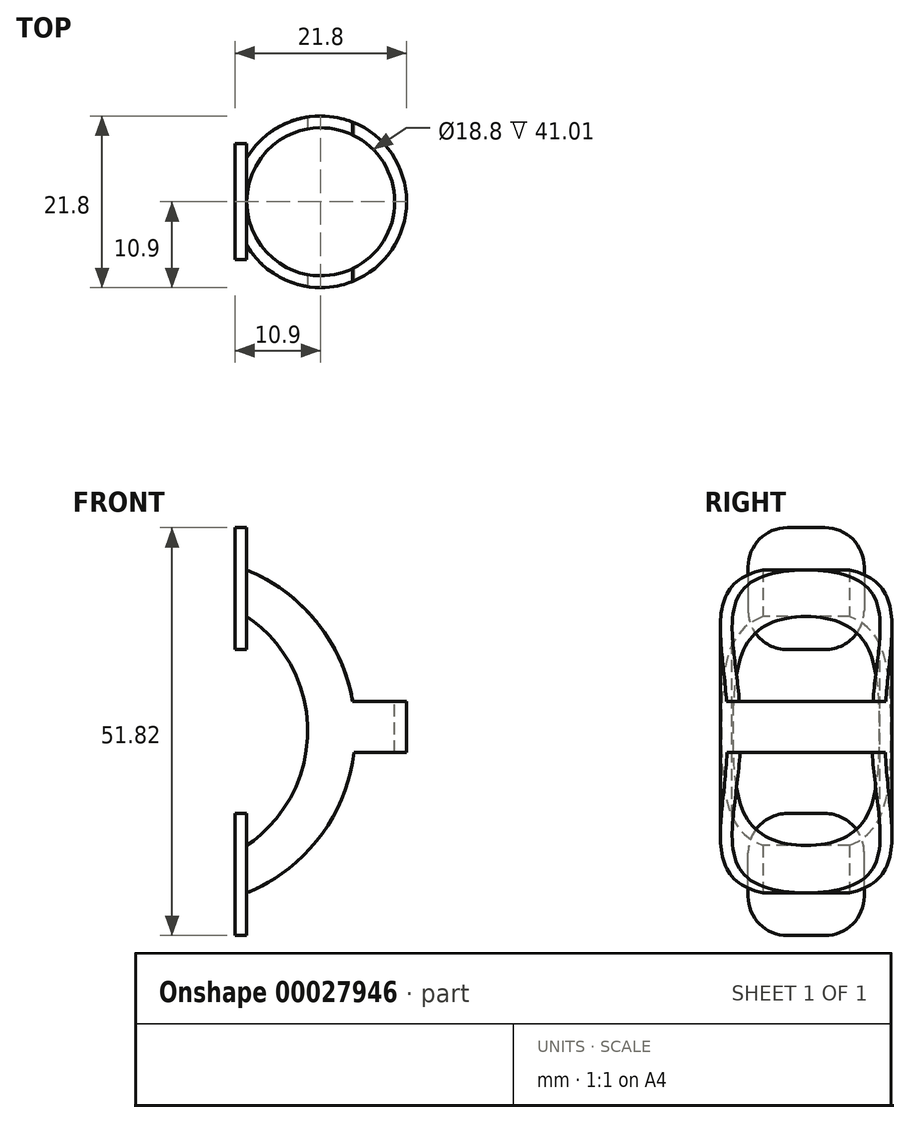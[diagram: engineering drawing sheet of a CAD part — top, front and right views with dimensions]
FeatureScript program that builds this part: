
annotation { "Feature Type Name" : "Feature", "Feature Type Description" : "" }
export const myFeature = defineFeature(function(context is Context, id is Id, definition is map)
    precondition{}
    {
        {
            var Q0;
            Q0=qCreatedBy(makeId("Top.planeOp"),FACE);
            var sketch = newSketch(context, id + "F0", { "sketchPlane" : qUnion([Q0])});
            skCircle(sketch, "E0", {"center": v(0, 0) * mm, "radius": 10.9 * mm});
            skSolve(sketch);
        }
        {
            var Q0;
            Q0 = qSketchRegion(id + "F0", true);
            extrude(context, id + "F1", {"entities" : qUnion([Q0]), "depth" : 42 * mm});
        }
        {
            var Q0;
            Q0=makeQuery(id+"F1.opExtrude","CAP_FACE",FACE,{"disambiguationData":[OSD([sQuery(id+"F0.wireOp",EDGE,"E0")])],"isStart":false});
            var sketch = newSketch(context, id + "F2", { "sketchPlane" : qUnion([Q0])});
            skCircle(sketch, "E1.0", {"center": v(0, 0) * mm, "radius": 9.4 * mm});
            skSolve(sketch);
        }
        {
            var Q0;
            Q0=makeQuery(id+"F2.imprint","IMPRINT",FACE,{"disambiguationData":[TD([[makeQuery(id+"F2.imprint","IMPRINT",EDGE,{"derivedFrom":sQuery(id+"F2.wireOp",EDGE,"E1.0")}),1.0]])]});
            extrude(context, id + "F3", {"entities" : qUnion([Q0]), "operationType" : NewBodyOperationType.REMOVE, "endBound" : BoundingType.THROUGH_ALL, "oppositeDirection" : true, "depth" : 25 * mm});
        }
        {
            var Q0;
            Q0=qCreatedBy(makeId("Front.planeOp"),FACE);
            cPlane(context, id + "F4", {"entities" : qUnion([Q0]), "cplaneType" : CPlaneType.OFFSET, "offset" : 10.9 * mm, "width" : 150 * mm, "height" : 150 * mm});
        }
        {
            var Q0;
            Q0=qCreatedBy(makeId("Front.planeOp"),FACE);
            var sketch = newSketch(context, id + "F5", { "sketchPlane" : qUnion([Q0])});
            skArc(sketch, "E2", {"start": v(-11.41, 5.25) * mm, "mid": v(-1.67, 21.04) * mm, "end": v(-11.54, 36.75) * mm});
            skLineSegment(sketch, "E3", {"start": v(-11.54, 36.75) * mm, "end": v(-11.41, 5.25) * mm});
            skSolve(sketch);
        }
        {
            var Q0;
            Q0=makeQuery(id+"F5.imprint","IMPRINT",FACE,{"disambiguationData":[TD([[makeQuery(id+"F5.imprint","IMPRINT",EDGE,{"derivedFrom":sQuery(id+"F5.wireOp",EDGE,"E2")}),1.0]])]});
            extrude(context, id + "F6", {"entities" : qUnion([Q0]), "operationType" : NewBodyOperationType.REMOVE, "oppositeDirection" : true, "depth" : 25 * mm, "symmetric" : true});
        }
        {
            var Q0;
            Q0=qCreatedBy(id+"F4.planeOp",FACE);
            var sketch = newSketch(context, id + "F7", { "sketchPlane" : qUnion([Q0])});
            skArc(sketch, "E4", {"start": v(-10.48, 0) * mm, "mid": v(-0.51, 7.01) * mm, "end": v(4.23, 18.24) * mm});
            skLineSegment(sketch, "E5", {"start": v(4.06, 24.74) * mm, "end": v(19.03, 24.74) * mm});
            skLineSegment(sketch, "E6", {"start": v(19.03, 24.74) * mm, "end": v(19.03, 18.24) * mm});
            skLineSegment(sketch, "E7", {"start": v(19.03, 18.24) * mm, "end": v(4.23, 18.24) * mm});
            skArc(sketch, "E8.trimOffspring", {"start": v(4.06, 24.74) * mm, "mid": v(-1.2, 35.63) * mm, "end": v(-11.4, 42.12) * mm});
            skLineSegment(sketch, "E9", {"start": v(-11.4, 42.12) * mm, "end": v(25.8, 42.12) * mm});
            skLineSegment(sketch, "E10", {"start": v(25.8, 42.12) * mm, "end": v(25.8, 0) * mm});
            skLineSegment(sketch, "E11", {"start": v(25.8, 0) * mm, "end": v(-10.48, 0) * mm});
            skSolve(sketch);
        }
        {
            var Q0;
            Q0=makeQuery(id+"F7.imprint","IMPRINT",FACE,{"disambiguationData":[TD([[makeQuery(id+"F7.imprint","IMPRINT",EDGE,{"derivedFrom":sQuery(id+"F7.wireOp",EDGE,"E4")}),-1.0]])]});
            extrude(context, id + "F8", {"entities" : qUnion([Q0]), "operationType" : NewBodyOperationType.REMOVE, "endBound" : BoundingType.THROUGH_ALL, "oppositeDirection" : true, "depth" : 25 * mm});
        }
        {
            var Q0;
            Q0=qCreatedBy(makeId("Right.planeOp"),FACE);
            cPlane(context, id + "F9", {"entities" : qUnion([Q0]), "cplaneType" : CPlaneType.OFFSET, "offset" : 10.9 * mm, "oppositeDirection" : true, "width" : 150 * mm, "height" : 150 * mm});
        }
        {
            var Q0;
            Q0=qCreatedBy(id+"F9.planeOp",FACE);
            var sketch = newSketch(context, id + "F10", { "sketchPlane" : qUnion([Q0])});
            skLineSegment(sketch, "E12.bottom", {"start": v(2.37, 46.8) * mm, "end": v(-2.38, 46.8) * mm});
            skLineSegment(sketch, "E12.top", {"start": v(2.37, 31.3) * mm, "end": v(-2.38, 31.3) * mm});
            skLineSegment(sketch, "E12.left", {"start": v(7.37, 41.8) * mm, "end": v(7.37, 36.3) * mm});
            skLineSegment(sketch, "E12.right", {"start": v(-7.38, 41.8) * mm, "end": v(-7.38, 36.3) * mm});
            skLineSegment(sketch, "E13", {"start": v(2.13, 39.05) * mm, "end": v(-2.85, 39.05) * mm, "construction": true});
            skLineSegment(sketch, "E14", {"start": v(0, 41.08) * mm, "end": v(0, 36.65) * mm, "construction": true});
            skPoint(sketch, "E15.visualSharp", {"position": v(7.37, 46.8) * mm});
            skArc(sketch, "E15.filletArc", {"start": v(7.37, 41.8) * mm, "mid": v(5.91, 45.33) * mm, "end": v(2.37, 46.8) * mm});
            skPoint(sketch, "E16.visualSharp", {"position": v(-7.38, 46.8) * mm});
            skArc(sketch, "E16.filletArc", {"start": v(-2.38, 46.8) * mm, "mid": v(-5.91, 45.33) * mm, "end": v(-7.38, 41.8) * mm});
            skPoint(sketch, "E17.visualSharp", {"position": v(-7.38, 31.3) * mm});
            skArc(sketch, "E17.filletArc", {"start": v(-7.38, 36.3) * mm, "mid": v(-5.91, 32.76) * mm, "end": v(-2.38, 31.3) * mm});
            skPoint(sketch, "E18.visualSharp", {"position": v(7.38, 31.3) * mm});
            skArc(sketch, "E18.filletArc", {"start": v(2.37, 31.3) * mm, "mid": v(5.91, 32.76) * mm, "end": v(7.37, 36.3) * mm});
            skLineSegment(sketch, "E19", {"start": v(0, 20.9) * mm, "end": v(4.83, 20.9) * mm, "construction": true});
            skLineSegment(sketch, "E20.MirrorCS", {"start": v(7.37, -0.02) * mm, "end": v(7.37, 5.48) * mm});
            skArc(sketch, "E21.MirrorCS", {"start": v(7.37, -0.02) * mm, "mid": v(5.91, -3.55) * mm, "end": v(2.37, -5.02) * mm});
            skLineSegment(sketch, "E22.MirrorCS", {"start": v(2.37, -5.02) * mm, "end": v(-2.38, -5.02) * mm});
            skArc(sketch, "E23.MirrorCS", {"start": v(-2.38, -5.02) * mm, "mid": v(-5.91, -3.55) * mm, "end": v(-7.38, -0.02) * mm});
            skLineSegment(sketch, "E24.MirrorCS", {"start": v(-7.38, -0.02) * mm, "end": v(-7.38, 5.48) * mm});
            skArc(sketch, "E25.MirrorCS", {"start": v(-7.38, 5.48) * mm, "mid": v(-5.91, 9.02) * mm, "end": v(-2.38, 10.48) * mm});
            skLineSegment(sketch, "E26.MirrorCS", {"start": v(2.37, 10.48) * mm, "end": v(-2.38, 10.48) * mm});
            skArc(sketch, "E27.MirrorCS", {"start": v(2.37, 10.48) * mm, "mid": v(5.91, 9.02) * mm, "end": v(7.37, 5.48) * mm});
            skSolve(sketch);
        }
        {
            var Q0;
            Q0=makeQuery(id+"F10.imprint","IMPRINT",FACE,{"disambiguationData":[TD([[makeQuery(id+"F10.imprint","IMPRINT",EDGE,{"derivedFrom":sQuery(id+"F10.wireOp",EDGE,"E12.bottom")}),1.0]])]});
            var Q1;
            Q1=makeQuery(id+"F10.imprint","IMPRINT",FACE,{"disambiguationData":[TD([[makeQuery(id+"F10.imprint","IMPRINT",EDGE,{"derivedFrom":sQuery(id+"F10.wireOp",EDGE,"E20.MirrorCS")}),1.0]])]});
            extrude(context, id + "F11", {"entities" : qUnion([Q0, Q1]), "operationType" : NewBodyOperationType.ADD, "depth" : 1.5 * mm});
        }
    });
